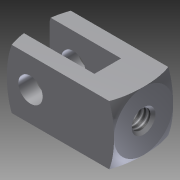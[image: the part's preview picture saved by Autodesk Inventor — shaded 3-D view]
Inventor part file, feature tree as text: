
AUTODESK INVENTOR PART (.ipt)
format: ipt  version: 2012 (Build 160160000, 160)  size: 179,712 bytes
history: native  units: in
note: dims shown in document units (in); Inventor stores cm internally (conversion verified against a paired STEP export)
features: other x126, sketch x7, hole x3, extrude x2, revolve x2
ambient origin geometry x8: Origin, YZ Plane, XZ Plane, XY Plane, X Axis, Y Axis, Z Axis, Center Point
bodies: Solid1 (feature_tree)
feature tree (140):
  extrude  "Extrusion1"  Depth=0.31in TaperAngle=0.0deg
  extrude  "Extrusion2"  TaperAngle=360.0deg  [1 undecoded]
  hole  "Drilling 1"  [1 undecoded]
  hole  "Drilling 2"  [1 undecoded]
  hole  "Drilling 3"  [1 undecoded]
  revolve  "Revolution1"  [1 undecoded]
  revolve  "Revolution2"  [1 undecoded]
  other  "th1_XY"
  other  "th1_YZ"
  other  "th1_ZX"
  other  "th1_X"
  other  "th1_Y"
  other  "th1_Z"
  other  "th1_Center"
  other  "th2_XY"
  other  "th2_YZ"
  other  "th2_ZX"
  other  "th2_X"
  other  "th2_Y"
  other  "th2_Z"
  other  "th2_Center"
  other  "rod_clevis_body_XY"
  other  "rod_clevis_body_YZ"
  other  "rod_clevis_body_ZX"
  other  "rod_clevis_body_X"
  other  "rod_clevis_body_Y"
  other  "rod_clevis_body_Z"
  other  "rod_clevis_body_Center"
  other  "piston_rod_clevis_XY"
  other  "piston_rod_clevis_YZ"
  other  "piston_rod_clevis_ZX"
  other  "piston_rod_clevis_X"
  other  "piston_rod_clevis_Y"
  other  "piston_rod_clevis_Z"
  other  "piston_rod_clevis_Center"
  other  "dummy_XY"
  other  "dummy_YZ"
  other  "dummy_ZX"
  other  "dummy_X"
  other  "dummy_Y"
  other  "dummy_Z"
  other  "dummy_Center"
  other  "l11_XY"
  other  "l11_YZ"
  other  "l11_ZX"
  other  "l11_X"
  other  "l11_Y"
  other  "l11_Z"
  other  "l11_Center"
  other  "l12_XY"
  other  "l12_YZ"
  other  "l12_ZX"
  other  "l12_X"
  other  "l12_Y"
  other  "l12_Z"
  other  "l12_Center"
  other  "l1_XY"
  other  "l1_YZ"
  other  "l1_ZX"
  other  "l1_X"
  other  "l1_Y"
  other  "l1_Z"
  other  "l1_Center"
  other  "h1_XY"
  other  "h1_YZ"
  other  "h1_ZX"
  other  "h1_X"
  other  "h1_Y"
  other  "h1_Z"
  other  "h1_Center"
  other  "l2_XY"
  other  "l2_YZ"
  other  "l2_ZX"
  other  "l2_X"
  other  "l2_Y"
  other  "l2_Z"
  other  "l2_Center"
  other  "h2_XY"
  other  "h2_YZ"
  other  "h2_ZX"
  other  "h2_X"
  other  "h2_Y"
  other  "h2_Z"
  other  "h2_Center"
  other  "w11_XY"
  other  "w11_YZ"
  other  "w11_ZX"
  other  "w11_X"
  other  "w11_Y"
  other  "w11_Z"
  other  "w11_Center"
  other  "w12_XY"
  other  "w12_YZ"
  other  "w12_ZX"
  other  "w12_X"
  other  "w12_Y"
  other  "w12_Z"
  other  "w12_Center"
  other  "l21_XY"
  other  "l21_YZ"
  other  "l21_ZX"
  other  "l21_X"
  other  "l21_Y"
  other  "l21_Z"
  other  "l21_Center"
  other  "l22_XY"
  other  "l22_YZ"
  other  "l22_ZX"
  other  "l22_X"
  other  "l22_Y"
  other  "l22_Z"
  other  "l22_Center"
  other  "w1_XY"
  other  "w1_YZ"
  other  "w1_ZX"
  other  "w1_X"
  other  "w1_Y"
  other  "w1_Z"
  other  "w1_Center"
  other  "w2_XY"
  other  "w2_YZ"
  other  "w2_ZX"
  other  "w2_X"
  other  "w2_Y"
  other  "w2_Z"
  other  "w2_Center"
  other  "to_cylinder_XY"
  other  "to_cylinder_YZ"
  other  "to_cylinder_ZX"
  other  "to_cylinder_X"
  other  "to_cylinder_Y"
  other  "to_cylinder_Z"
  other  "to_cylinder_Center"
  sketch  "Sketch_1"  dims[d0=0.31in d1=0.0in d2=0.31in d3=0.0in]
  sketch  "Sketch_2"  dims[d4=0.0979in d5=0.18in d6=0.125in d7=0.25in d8=90.0deg d9=0.18in d10=0.0in]
  sketch  "Sketch3"  dims[d11=0.0995in d12=0.75in d13=0.375in d14=0.25in d15=0.5635in d16=0.008in d17=0.0in]
  sketch  "Sketch4"  dims[d18=0.1275in d19=0.75in d20=0.375in d21=0.25in d22=0.5635in d23=0.31in d24=0.0in d25=360.0deg]
  sketch  "Sketch5"  dims[d26=360.0deg]
  sketch  "Sketch_9"
  sketch  "Sketch_10"
note: 6 required parameter values undecoded (feature->parameter linkage not recoverable at this tier; creation-order binding heuristic only, values carry confidence <= 0.55)
